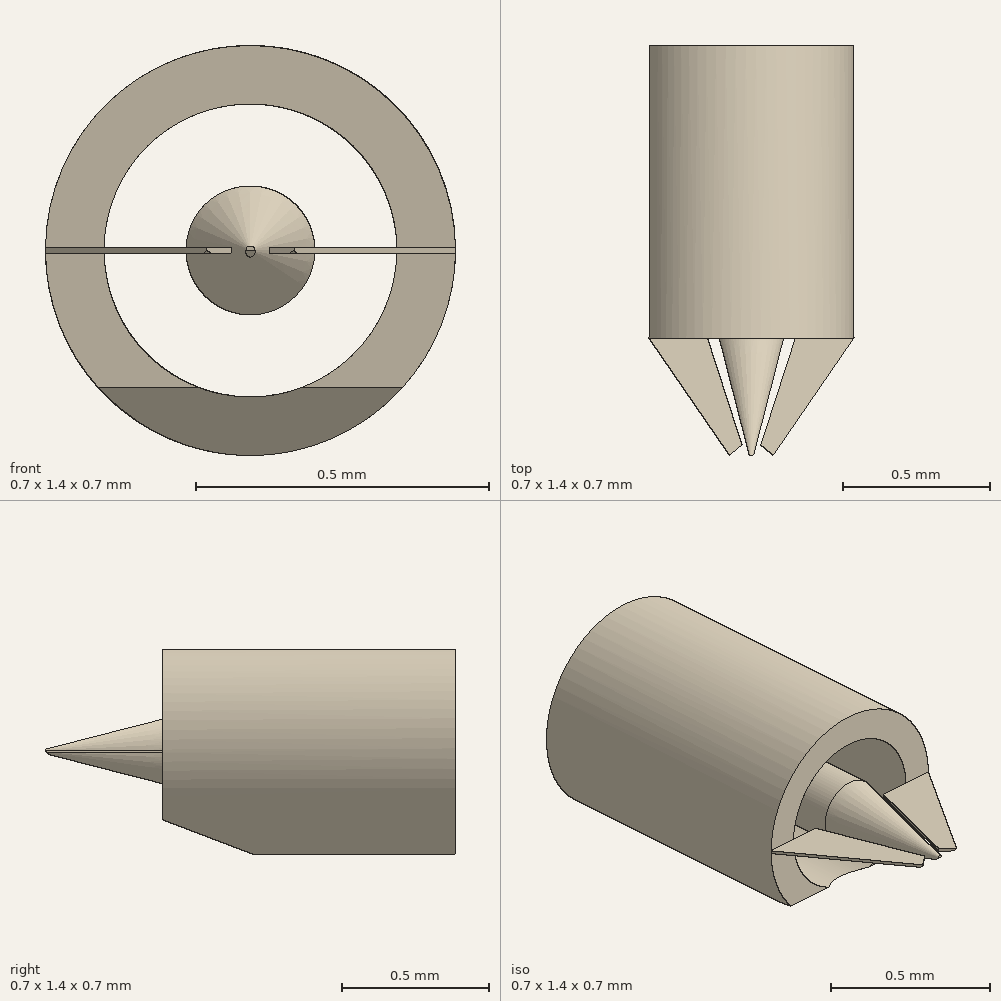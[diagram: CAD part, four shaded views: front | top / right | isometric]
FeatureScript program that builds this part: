
annotation { "Feature Type Name" : "Feature", "Feature Type Description" : "" }
export const myFeature = defineFeature(function(context is Context, id is Id, definition is map)
    precondition{}
    {
        {
            var Q0;
            Q0=qCreatedBy(makeId("Front.planeOp"),FACE);
            var sketch = newSketch(context, id + "F0", { "sketchPlane" : qUnion([Q0])});
            skCircle(sketch, "E0", {"center": v(0, 0) * mm, "radius": 0.11 * mm});
            skCircle(sketch, "E1", {"center": v(0, 0) * mm, "radius": 0.25 * mm});
            skCircle(sketch, "E2", {"center": v(0, 0) * mm, "radius": 0.35 * mm});
            skSolve(sketch);
        }
        {
            var Q0;
            Q0=makeQuery(id+"F0.imprint","IMPRINT",FACE,{"disambiguationData":[TD([[makeQuery(id+"F0.imprint","IMPRINT",EDGE,{"derivedFrom":sQuery(id+"F0.wireOp",EDGE,"E1")}),-1.0]])]});
            var Q1;
            Q1=makeQuery(id+"F0.imprint","IMPRINT",FACE,{"disambiguationData":[TD([[makeQuery(id+"F0.imprint","IMPRINT",EDGE,{"derivedFrom":sQuery(id+"F0.wireOp",EDGE,"E0")}),1.0]])]});
            extrude(context, id + "F1", {"entities" : qUnion([Q0, Q1]), "oppositeDirection" : true, "depth" : 1 * mm, "offsetDistance" : 25 * mm});
        }
        {
            var Q0;
            Q0=qCreatedBy(makeId("Top.planeOp"),FACE);
            var sketch = newSketch(context, id + "F2", { "sketchPlane" : qUnion([Q0])});
            skLineSegment(sketch, "E3", {"start": v(0.35, 0) * mm, "end": v(0.35, 1) * mm});
            skLineSegment(sketch, "E4", {"start": v(-0.35, 1) * mm, "end": v(-0.35, 0) * mm});
            skLineSegment(sketch, "E5", {"start": v(0.11, 0) * mm, "end": v(0.11, 1) * mm});
            skLineSegment(sketch, "E6", {"start": v(-0.11, 1) * mm, "end": v(-0.11, 0) * mm});
            skLineSegment(sketch, "E7", {"start": v(0, 0.93) * mm, "end": v(0, -1.02) * mm});
            skLineSegment(sketch, "E8", {"start": v(0.25, 0) * mm, "end": v(0.25, 1) * mm});
            skLineSegment(sketch, "E9", {"start": v(-0.25, 1) * mm, "end": v(-0.25, 0) * mm});
            skLineSegment(sketch, "E10", {"start": v(-0.11, 0) * mm, "end": v(0, -0.4) * mm});
            skLineSegment(sketch, "E11", {"start": v(0, -0.4) * mm, "end": v(0, -0.4) * mm});
            skLineSegment(sketch, "E12", {"start": v(0.1, 0) * mm, "end": v(0, -0.4) * mm});
            skLineSegment(sketch, "E13", {"start": v(-1.83, -0.4) * mm, "end": v(1.75, -0.4) * mm, "construction": true});
            skLineSegment(sketch, "E14", {"start": v(0.25, 0) * mm, "end": v(0.35, 0) * mm});
            skLineSegment(sketch, "E15", {"start": v(-0.11, 0) * mm, "end": v(0.11, 0) * mm});
            skLineSegment(sketch, "E16.MirrorCS", {"start": v(-0.25, 0) * mm, "end": v(-0.35, 0) * mm});
            skLineSegment(sketch, "E17", {"start": v(-0.35, 0) * mm, "end": v(-0.15, 0) * mm});
            skLineSegment(sketch, "E18", {"start": v(-0.15, 0) * mm, "end": v(-0.03, -0.37) * mm});
            skLineSegment(sketch, "E19", {"start": v(-0.03, -0.37) * mm, "end": v(-0.08, -0.4) * mm});
            skLineSegment(sketch, "E20", {"start": v(-0.07, -0.4) * mm, "end": v(-0.35, 0) * mm});
            skLineSegment(sketch, "E21.MirrorCS", {"start": v(0.07, -0.4) * mm, "end": v(0.35, 0) * mm});
            skLineSegment(sketch, "E22.MirrorCS", {"start": v(0.03, -0.37) * mm, "end": v(0.08, -0.4) * mm});
            skLineSegment(sketch, "E23.MirrorCS", {"start": v(0.15, 0) * mm, "end": v(0.03, -0.37) * mm});
            skLineSegment(sketch, "E24.MirrorCS", {"start": v(0.35, 0) * mm, "end": v(0.15, 0) * mm});
            skSolve(sketch);
        }
        {
            var Q0;
            {var subQ1=sQuery(id+"F2.wireOp",EDGE,"E21.MirrorCS");Q0=makeQuery(id+"F2.imprint","IMPRINT",FACE,{"disambiguationData":[TD([[makeQuery(id+"F2.imprint","IMPRINT",EDGE,{"derivedFrom":subQ1}),1.0]])]});}
            var Q1;
            {var subQ0=sQuery(id+"F2.wireOp",EDGE,"E18");Q1=makeQuery(id+"F2.imprint","IMPRINT",FACE,{"disambiguationData":[TD([[makeQuery(id+"F2.imprint","IMPRINT",EDGE,{"derivedFrom":subQ0}),-1.0]])]});}
            extrude(context, id + "F3", {"entities" : qUnion([Q0, Q1]), "operationType" : NewBodyOperationType.ADD, "endBound" : BoundingType.SYMMETRIC, "depth" : 0.01 * mm, "offsetDistance" : 25 * mm});
        }
        {
            var Q0;
            {var subQ5=sQuery(id+"F2.wireOp",EDGE,"E12");Q0=makeQuery(id+"F2.imprint","IMPRINT",FACE,{"disambiguationData":[TD([[makeQuery(id+"F2.imprint","IMPRINT",EDGE,{"derivedFrom":subQ5}),-1.0]])]});}
            var Q1;
            Q1=sQuery(id+"F2.wireOp",EDGE,"E7");
            revolve(context, id + "F4", {"operationType" : NewBodyOperationType.ADD, "entities" : qUnion([Q0]), "axis" : qUnion([Q1]), "revolveType" : RevolveType.FULL});
        }
        {
            var Q0;
            Q0=qCreatedBy(makeId("Right.planeOp"),FACE);
            var sketch = newSketch(context, id + "F5", { "sketchPlane" : qUnion([Q0])});
            skLineSegment(sketch, "E25", {"start": v(-0.43, 0.02) * mm, "end": v(-0.17, -0.17) * mm});
            skPoint(sketch, "E26.0", {"position": v(-0.4, 0) * mm});
            skLineSegment(sketch, "E27", {"start": v(-0.17, -0.17) * mm, "end": v(0.4, -0.39) * mm});
            skLineSegment(sketch, "E28", {"start": v(0.4, -0.39) * mm, "end": v(0.07, -0.8) * mm});
            skLineSegment(sketch, "E29", {"start": v(0.07, -0.8) * mm, "end": v(-0.43, 0.02) * mm});
            skSolve(sketch);
        }
        {
            var Q0;
            Q0 = qSketchRegion(id + "F5", true);
            extrude(context, id + "F6", {"entities" : qUnion([Q0]), "operationType" : NewBodyOperationType.REMOVE, "endBound" : BoundingType.SYMMETRIC, "oppositeDirection" : true, "depth" : 25 * mm, "offsetDistance" : 25 * mm});
        }
    });
